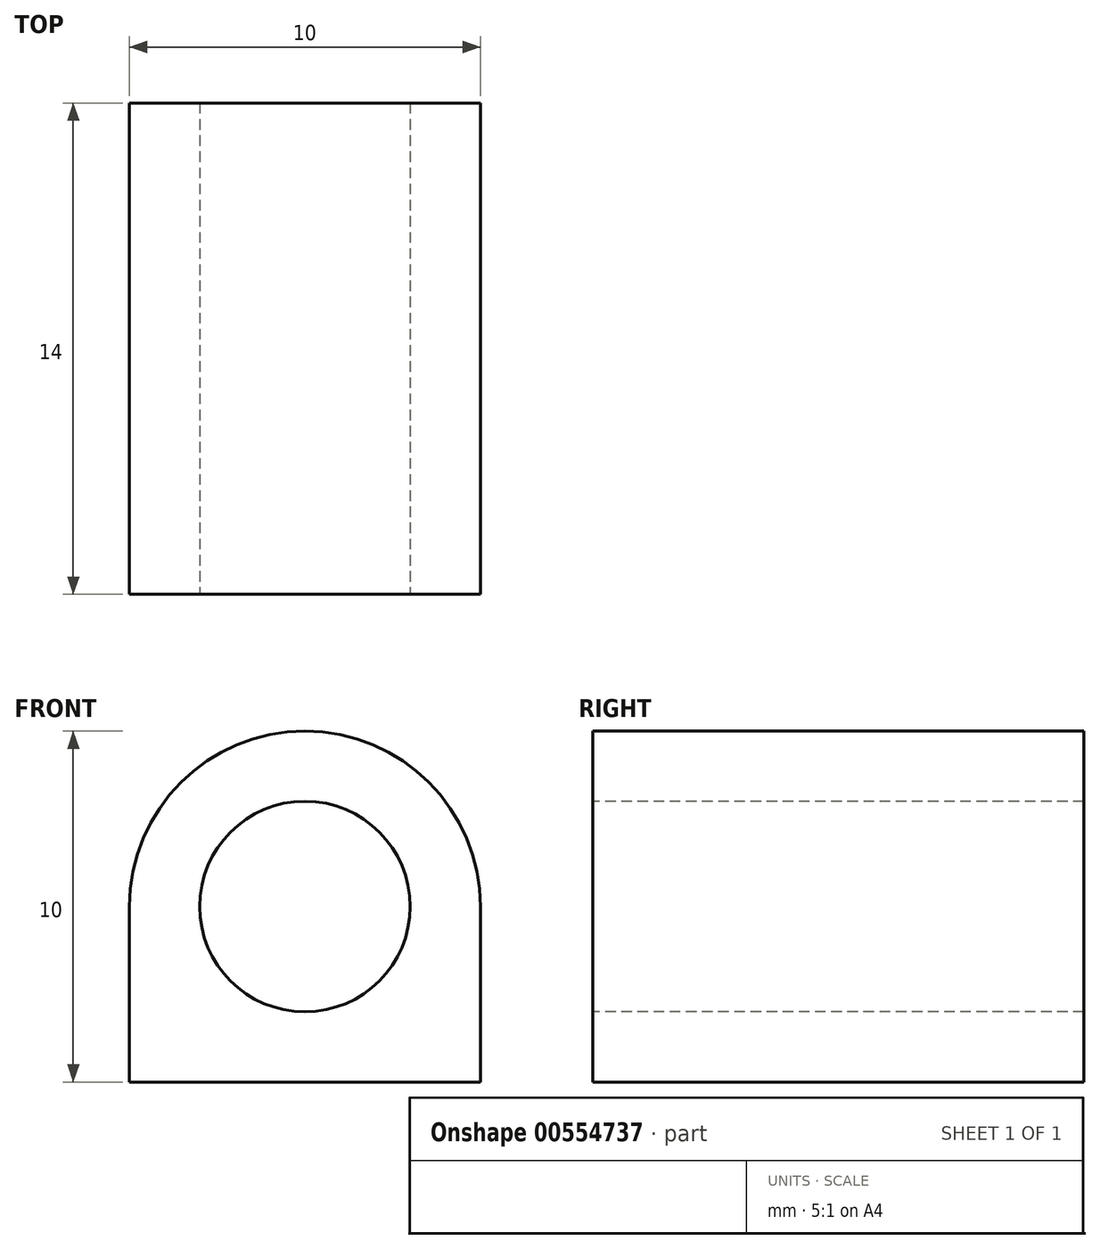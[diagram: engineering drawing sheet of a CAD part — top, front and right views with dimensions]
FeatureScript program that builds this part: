
annotation { "Feature Type Name" : "Feature", "Feature Type Description" : "" }
export const myFeature = defineFeature(function(context is Context, id is Id, definition is map)
    precondition{}
    {
        {
            var Q0;
            Q0=qCreatedBy(makeId("Top.planeOp"),FACE);
            var sketch = newSketch(context, id + "F0", { "sketchPlane" : qUnion([Q0])});
            skLineSegment(sketch, "E0.bottom", {"start": v(5, 7) * mm, "end": v(-5, 7) * mm});
            skLineSegment(sketch, "E0.top", {"start": v(5, -7) * mm, "end": v(-5, -7) * mm});
            skLineSegment(sketch, "E0.left", {"start": v(5, 7) * mm, "end": v(5, -7) * mm});
            skLineSegment(sketch, "E0.right", {"start": v(-5, 7) * mm, "end": v(-5, -7) * mm});
            skPoint(sketch, "E0.middle", {"position": v(0, 0) * mm});
            skSolve(sketch);
        }
        {
            var Q0;
            Q0=makeQuery(id+"F0.imprint","IMPRINT",FACE,{"disambiguationData":[TD([[makeQuery(id+"F0.imprint","IMPRINT",EDGE,{"derivedFrom":sQuery(id+"F0.wireOp",EDGE,"E0.bottom")}),1.0]])]});
            extrude(context, id + "F1", {"entities" : qUnion([Q0]), "depth" : 10 * mm, "offsetDistance" : 25 * mm});
        }
        {
            var Q0;
            Q0=makeQuery(id+"F1.opExtrude","SWEPT_FACE",FACE,{"disambiguationData":[OSD([sQuery(id+"F0.wireOp",EDGE,"E0.top")])]});
            var sketch = newSketch(context, id + "F2", { "sketchPlane" : qUnion([Q0])});
            skCircle(sketch, "E1", {"center": v(0, 5) * mm, "radius": 3 * mm});
            skPoint(sketch, "E1.centerSnap0", {"position": v(0, 10) * mm});
            skPoint(sketch, "E1.centerSnap1", {"position": v(-5, 5) * mm});
            skArc(sketch, "E2", {"start": v(0, 10) * mm, "mid": v(-3.54, 8.54) * mm, "end": v(-5, 5) * mm});
            skArc(sketch, "E3", {"start": v(5, 5) * mm, "mid": v(3.54, 8.54) * mm, "end": v(0, 10) * mm});
            skSolve(sketch);
        }
        {
            var Q0;
            Q0=makeQuery(id+"F2.imprint","IMPRINT",FACE,{"disambiguationData":[TD([[makeQuery(id+"F2.imprint","IMPRINT",EDGE,{"derivedFrom":sQuery(id+"F2.wireOp",EDGE,"E1")}),1.0]])]});
            var Q1;
            {var subQ0=sQuery(id+"F2.wireOp",EDGE,"E2");Q1=makeQuery(id+"F2.imprint","IMPRINT",FACE,{"disambiguationData":[TD([[makeQuery(id+"F2.imprint","IMPRINT",EDGE,{"derivedFrom":subQ0}),-1.0]])]});}
            var Q2;
            {var subQ0=sQuery(id+"F2.wireOp",EDGE,"E3");Q2=makeQuery(id+"F2.imprint","IMPRINT",FACE,{"disambiguationData":[TD([[makeQuery(id+"F2.imprint","IMPRINT",EDGE,{"derivedFrom":subQ0}),-1.0]])]});}
            extrude(context, id + "F3", {"entities" : qUnion([Q0, Q1, Q2]), "operationType" : NewBodyOperationType.REMOVE, "endBound" : BoundingType.THROUGH_ALL, "oppositeDirection" : true, "depth" : 25 * mm, "offsetDistance" : 25 * mm});
        }
    });
